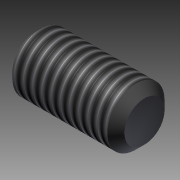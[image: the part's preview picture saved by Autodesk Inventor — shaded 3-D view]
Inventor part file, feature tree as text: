
AUTODESK INVENTOR PART (.ipt)
format: ipt  version: 2016 (Build 200138000, 138)  size: 130,048 bytes
history: native  units: mm
features: other x7, sketch x3, revolve x2, thread x1, extrude x1
ambient origin geometry x8: Origin, YZ Plane, XZ Plane, XY Plane, X Axis, Y Axis, Z Axis, Center Point
bodies: Solid1 (feature_tree)
feature tree (14):
  revolve  "Revolution1"  [1 undecoded]
  thread  "Thread1"  [1 undecoded]
  extrude  "Extrusion1"  TaperAngle=0.0deg  [1 undecoded]
  revolve  "Revolution2"  [1 undecoded]
  other  "CP_XY"
  other  "CP_YZ"
  other  "CP_ZX"
  other  "CP_X"
  other  "CP_Y"
  other  "CP_Z"
  other  "CP_Center"
  sketch  "Sketch_1"  dims[d0=360.0deg d1=8.2595mm d2=0.0mm d3=2.0mm d4=0.0mm]
  sketch  "Sketch_2"  dims[d5=360.0deg d6=0.0mm]
  sketch  "Sketch_3"
note: 4 required parameter values undecoded (feature->parameter linkage not recoverable at this tier; creation-order binding heuristic only, values carry confidence <= 0.55)